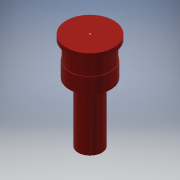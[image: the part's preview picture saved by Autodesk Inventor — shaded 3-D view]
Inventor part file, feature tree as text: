
AUTODESK INVENTOR PART (.ipt)
format: ipt  version: 2019 (Build 230136000, 136)  size: 120,832 bytes
history: native  units: in
note: dims shown in document units (in); Inventor stores cm internally (conversion verified against a paired STEP export)
features: sketch x5, extrude x4
ambient origin geometry x8: Origin, YZ Plane, XZ Plane, XY Plane, X Axis, Y Axis, Z Axis, Center Point
bodies: Solid1 (feature_tree)
feature tree (9):
  extrude  "Extrusion1"  Depth=1.9685in TaperAngle=0.0deg
  extrude  "Extrusion2"  Depth=0.5118in TaperAngle=0.0deg
  extrude  "Extrusion3"  Depth=0.5906in TaperAngle=0.0deg
  extrude  "Extrusion4"  Depth=0.1575in TaperAngle=0.0deg
  sketch  "Sketch5"
  sketch  "Sketch1"  dims[d0=0.7874in d1=1.9685in d2=0.0in]
  sketch  "Sketch2"  dims[d3=1.378in d4=0.5118in d5=0.0in]
  sketch  "Sketch3"  dims[d6=1.3386in d7=0.5906in d8=0.0in]
  sketch  "Sketch4"  dims[d9=1.5748in d10=0.1575in d11=0.0in]
